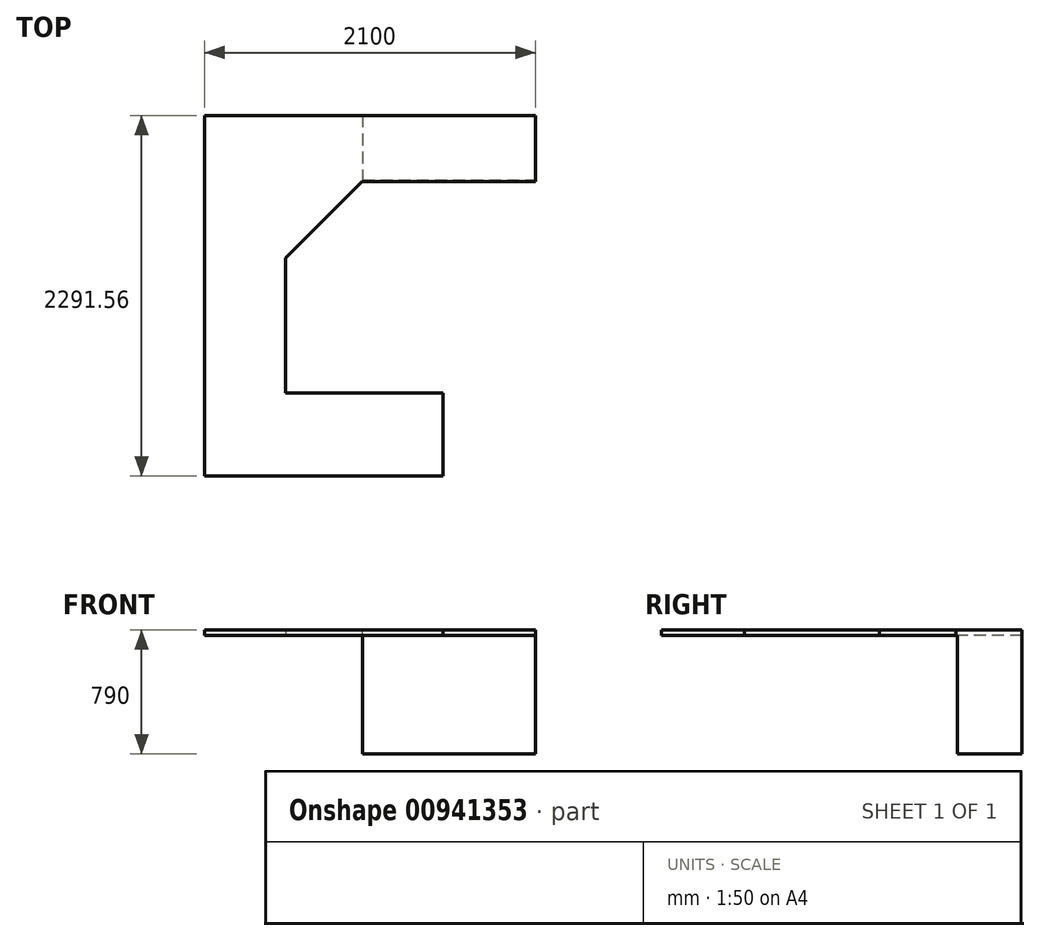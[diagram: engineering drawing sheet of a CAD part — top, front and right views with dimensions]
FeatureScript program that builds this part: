
annotation { "Feature Type Name" : "Feature", "Feature Type Description" : "" }
export const myFeature = defineFeature(function(context is Context, id is Id, definition is map)
    precondition{}
    {
        {
            var Q0;
            Q0=qCreatedBy(makeId("Top.planeOp"),FACE);
            var sketch = newSketch(context, id + "F0", { "sketchPlane" : qUnion([Q0])});
            skLineSegment(sketch, "E0.bottom", {"start": v(-1097, 0) * mm, "end": v(0, 0) * mm});
            skLineSegment(sketch, "E0.top", {"start": v(-1097, -410) * mm, "end": v(0, -410) * mm});
            skLineSegment(sketch, "E0.left", {"start": v(-1097, 0) * mm, "end": v(-1097, -410) * mm});
            skLineSegment(sketch, "E0.right", {"start": v(0, 0) * mm, "end": v(0, -410) * mm});
            skSolve(sketch);
        }
        {
            var Q0;
            Q0=makeQuery(id+"F0.imprint","IMPRINT",FACE,{"disambiguationData":[TD([[makeQuery(id+"F0.imprint","IMPRINT",EDGE,{"derivedFrom":sQuery(id+"F0.wireOp",EDGE,"E0.bottom")}),-1.0]])]});
            extrude(context, id + "F1", {"entities" : qUnion([Q0]), "depth" : 755 * mm, "offsetDistance" : 25 * mm});
        }
        {
            var Q0;
            Q0=makeQuery(id+"F1.opExtrude","CAP_FACE",FACE,{"disambiguationData":[OSD([sQuery(id+"F0.wireOp",EDGE,"E0.bottom"),sQuery(id+"F0.wireOp",EDGE,"E0.top"),sQuery(id+"F0.wireOp",EDGE,"E0.left"),sQuery(id+"F0.wireOp",EDGE,"E0.right")])],"isStart":false});
            var sketch = newSketch(context, id + "F2", { "sketchPlane" : qUnion([Q0])});
            skLineSegment(sketch, "E1.bottom", {"start": v(0, 0) * mm, "end": v(-1100, 0) * mm});
            skLineSegment(sketch, "E1.top", {"start": v(0, -420) * mm, "end": v(-1100, -420) * mm});
            skLineSegment(sketch, "E1.left", {"start": v(0, 0) * mm, "end": v(0, -420) * mm});
            skLineSegment(sketch, "E1.right", {"start": v(-1100, 0) * mm, "end": v(-1100, -420) * mm});
            skLineSegment(sketch, "E2.bottom", {"start": v(-1585, -906.56) * mm, "end": v(-2100, -906.56) * mm});
            skLineSegment(sketch, "E2.top", {"start": v(-1585, -1761.56) * mm, "end": v(-2100, -1761.56) * mm});
            skLineSegment(sketch, "E2.left", {"start": v(-1585, -906.56) * mm, "end": v(-1585, -1761.56) * mm});
            skLineSegment(sketch, "E2.right", {"start": v(-2100, -906.56) * mm, "end": v(-2100, -1761.56) * mm});
            skLineSegment(sketch, "E3.bottom", {"start": v(-2100, -1761.56) * mm, "end": v(-585, -1761.56) * mm});
            skLineSegment(sketch, "E3.top", {"start": v(-2100, -2291.56) * mm, "end": v(-585, -2291.56) * mm});
            skLineSegment(sketch, "E3.left", {"start": v(-2100, -2291.56) * mm, "end": v(-2100, -1761.56) * mm});
            skLineSegment(sketch, "E3.right", {"start": v(-585, -2291.56) * mm, "end": v(-585, -1761.56) * mm});
            skLineSegment(sketch, "E4", {"start": v(-1585, -906.56) * mm, "end": v(-1100, -420) * mm});
            skLineSegment(sketch, "E5", {"start": v(-1100, 0) * mm, "end": v(-2100, 0) * mm});
            skLineSegment(sketch, "E6", {"start": v(-2100, 0) * mm, "end": v(-2100, -906.56) * mm});
            skSolve(sketch);
        }
        {
            var Q0;
            {var subQ0=makeQuery(id+"F2.imprint","IMPRINT",EDGE,{"derivedFrom":sQuery(id+"F2.wireOp",EDGE,"E2.bottom")});var subQ1=makeQuery(id+"F2.imprint","IMPRINT",EDGE,{"derivedFrom":sQuery(id+"F2.wireOp",EDGE,"E2.top")});var subQ3=sQuery(id+"F2.wireOp",EDGE,"E1.right");var subQ4=makeQuery(id+"F2.imprint","IMPRINT",EDGE,{"derivedFrom":subQ3});var subQ6=makeQuery(id+"F1.opExtrude","CAP_EDGE",EDGE,{"disambiguationData":[OSD([sQuery(id+"F0.wireOp",EDGE,"E0.top")])],"isStart":false});var subQ8=sQuery(id+"F2.wireOp",EDGE,"E1.top");var subQ12=makeQuery(id+"F2.imprint","IMPRINT",EDGE,{"derivedFrom":subQ6});Q0=qUnion([makeQuery(id+"F2.imprint","IMPRINT",FACE,{"disambiguationData":[TD([[subQ12,1.0]])]}),makeQuery(id+"F2.imprint","IMPRINT",FACE,{"disambiguationData":[TD([[subQ1,1.0]])]}),makeQuery(id+"F2.imprint","IMPRINT",FACE,{"disambiguationData":[TD([[makeQuery(id+"F2.imprint","IMPRINT",EDGE,{"derivedFrom":subQ8}),-1.0]])]}),makeQuery(id+"F2.imprint","IMPRINT",FACE,{"disambiguationData":[TD([[subQ4,-1.0]])]}),makeQuery(id+"F2.imprint","IMPRINT",FACE,{"disambiguationData":[TD([[subQ0,1.0]])]})]);}
            extrude(context, id + "F3", {"entities" : qUnion([Q0]), "operationType" : NewBodyOperationType.ADD, "depth" : 35 * mm, "offsetDistance" : 25 * mm});
        }
        {
            var Q0;
            Q0=qCreatedBy(makeId("Front.planeOp"),FACE);
            var sketch = newSketch(context, id + "F4", { "sketchPlane" : qUnion([Q0])});
            skLineSegment(sketch, "E7", {"start": v(-1097, 0) * mm, "end": v(-2100, 0) * mm, "construction": true});
            skLineSegment(sketch, "E8", {"start": v(-2100, 755) * mm, "end": v(-2100, 0) * mm, "construction": true});
            skSolve(sketch);
        }
    });
